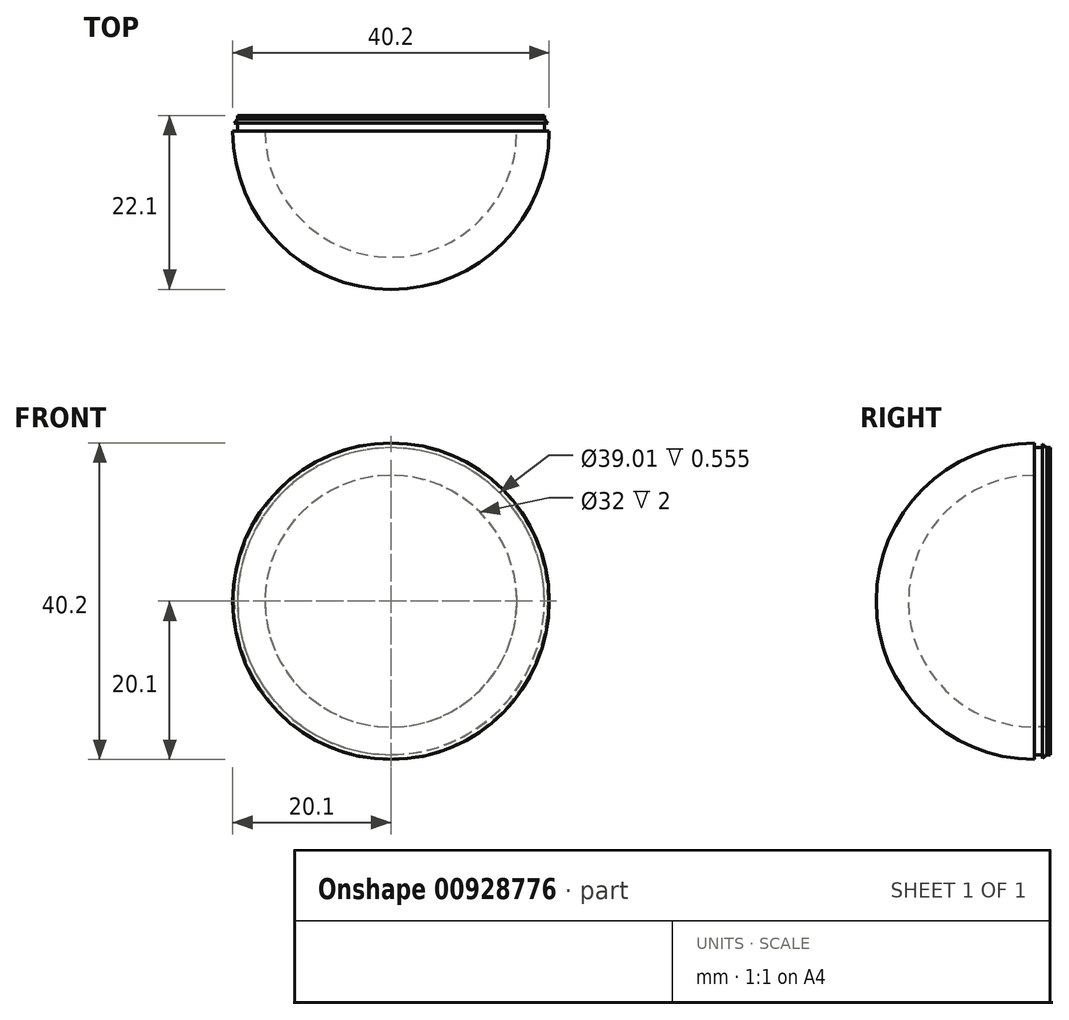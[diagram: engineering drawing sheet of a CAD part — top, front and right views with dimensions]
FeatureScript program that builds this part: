
annotation { "Feature Type Name" : "Feature", "Feature Type Description" : "" }
export const myFeature = defineFeature(function(context is Context, id is Id, definition is map)
    precondition{}
    {
        {
            var Q0;
            Q0=qCreatedBy(makeId("Front.planeOp"),FACE);
            var sketch = newSketch(context, id + "F0", { "sketchPlane" : qUnion([Q0])});
            skLineSegment(sketch, "E0", {"start": v(0, 20.1) * mm, "end": v(0, -20.1) * mm});
            skArc(sketch, "E1", {"start": v(0, -20.1) * mm, "mid": v(20.1, 0) * mm, "end": v(0, 20.1) * mm});
            skPoint(sketch, "E2.orphan", {"position": v(0, 41.64) * mm});
            skSolve(sketch);
        }
        {
            var Q0;
            Q0=makeQuery(id+"F0.imprint","IMPRINT",FACE,{"disambiguationData":[TD([[makeQuery(id+"F0.imprint","IMPRINT",EDGE,{"derivedFrom":sQuery(id+"F0.wireOp",EDGE,"E0")}),1.0]])]});
            var Q1;
            Q1=sQuery(id+"F0.wireOp",EDGE,"E0");
            revolve(context, id + "F1", {"surfaceOperationType" : NewSurfaceOperationType.NEW, "entities" : qUnion([Q0]), "axis" : qUnion([Q1]), "revolveType" : RevolveType.ONE_DIRECTION, "angle" : 180 * degree});
        }
        {
            var Q0;
            Q0=qCreatedBy(makeId("Front.planeOp"),FACE);
            var sketch = newSketch(context, id + "F2", { "sketchPlane" : qUnion([Q0])});
            skArc(sketch, "E3", {"start": v(0, 16) * mm, "mid": v(-16, 0) * mm, "end": v(0, -16) * mm});
            skLineSegment(sketch, "E4", {"start": v(0, 0) * mm, "end": v(0, 16) * mm});
            skLineSegment(sketch, "E5", {"start": v(0, 0) * mm, "end": v(0, -16) * mm});
            skCircle(sketch, "E6", {"center": v(0, 0) * mm, "radius": 16 * mm});
            skSolve(sketch);
        }
        {
            var Q0;
            Q0=qCreatedBy(makeId("Front.planeOp"),FACE);
            var sketch = newSketch(context, id + "F3", { "sketchPlane" : qUnion([Q0])});
            skCircle(sketch, "E7", {"center": v(0, 0) * mm, "radius": 19.5 * mm});
            skCircle(sketch, "E8", {"center": v(0, 0) * mm, "radius": 16 * mm});
            skSolve(sketch);
        }
        {
            var Q0;
            Q0 = qSketchRegion(id + "F3", true);
            extrude(context, id + "F4", {"entities" : qUnion([Q0]), "operationType" : NewBodyOperationType.ADD, "oppositeDirection" : true, "depth" : 2 * mm, "offsetDistance" : 25 * mm});
        }
        {
            var Q0;
            Q0=qCreatedBy(makeId("Right.planeOp"),FACE);
            var sketch = newSketch(context, id + "F5", { "sketchPlane" : qUnion([Q0])});
            skLineSegment(sketch, "E9", {"start": v(1.57, 19.5) * mm, "end": v(1.02, 19.5) * mm});
            skLineSegment(sketch, "E10", {"start": v(1.02, 19.5) * mm, "end": v(1.02, 19.94) * mm});
            skLineSegment(sketch, "E11", {"start": v(1.02, 19.94) * mm, "end": v(1.57, 19.5) * mm});
            skLineSegment(sketch, "E12", {"start": v(0, 0) * mm, "end": v(-10.74, 0) * mm});
            skSolve(sketch);
        }
        {
            var Q0;
            Q0=makeQuery(id+"F5.imprint","IMPRINT",FACE,{"disambiguationData":[TD([[makeQuery(id+"F5.imprint","IMPRINT",EDGE,{"derivedFrom":sQuery(id+"F5.wireOp",EDGE,"E9")}),-1.0]])]});
            var Q1;
            Q1=sQuery(id+"F5.wireOp",EDGE,"E12");
            revolve(context, id + "F6", {"surfaceOperationType" : NewSurfaceOperationType.NEW, "entities" : qUnion([Q0]), "axis" : qUnion([Q1]), "revolveType" : RevolveType.FULL});
        }
        {
            var Q0;
            {var subQ0=sQuery(id+"F2.wireOp",EDGE,"E4");Q0=makeQuery(id+"F2.imprint","IMPRINT",FACE,{"disambiguationData":[TD([[makeQuery(id+"F2.imprint","IMPRINT",EDGE,{"derivedFrom":subQ0}),-1.0]])]});}
            var Q1;
            Q1=sQuery(id+"F2.wireOp",EDGE,"E4");
            revolve(context, id + "F7", {"operationType" : NewBodyOperationType.REMOVE, "surfaceOperationType" : NewSurfaceOperationType.NEW, "entities" : qUnion([Q0]), "axis" : qUnion([Q1]), "revolveType" : RevolveType.FULL, "oppositeDirection" : true});
        }
    });
